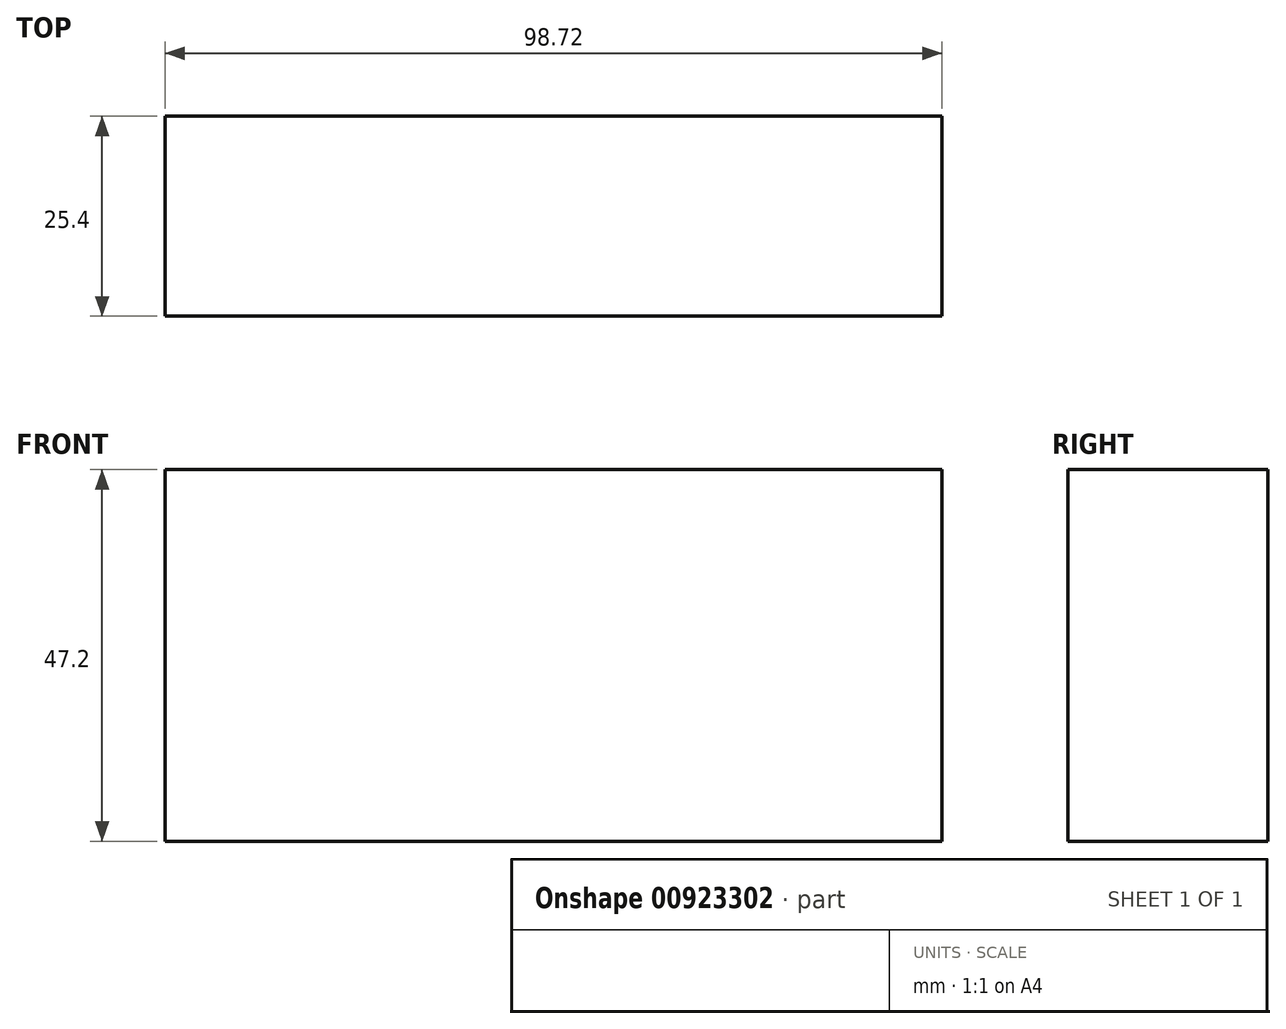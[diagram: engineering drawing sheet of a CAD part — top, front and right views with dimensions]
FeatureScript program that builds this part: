
annotation { "Feature Type Name" : "Feature", "Feature Type Description" : "" }
export const myFeature = defineFeature(function(context is Context, id is Id, definition is map)
    precondition{}
    {
        {
            var Q0;
            Q0=qCreatedBy(makeId("Front.planeOp"),FACE);
            var sketch = newSketch(context, id + "F0", { "sketchPlane" : qUnion([Q0])});
            skLineSegment(sketch, "E0.bottom", {"start": v(-50.5, 51.37) * mm, "end": v(48.2, 51.37) * mm});
            skLineSegment(sketch, "E0.top", {"start": v(-50.5, 4.17) * mm, "end": v(48.2, 4.17) * mm});
            skLineSegment(sketch, "E0.left", {"start": v(-50.5, 51.37) * mm, "end": v(-50.5, 4.17) * mm});
            skLineSegment(sketch, "E0.right", {"start": v(48.2, 51.37) * mm, "end": v(48.2, 4.17) * mm});
            skSolve(sketch);
        }
        {
            var Q0;
            Q0 = qSketchRegion(id + "F0", true);
            extrude(context, id + "F1", {"entities" : qUnion([Q0]), "depth" : 25.4 * mm, "offsetDistance" : 25.4 * mm});
        }
    });
